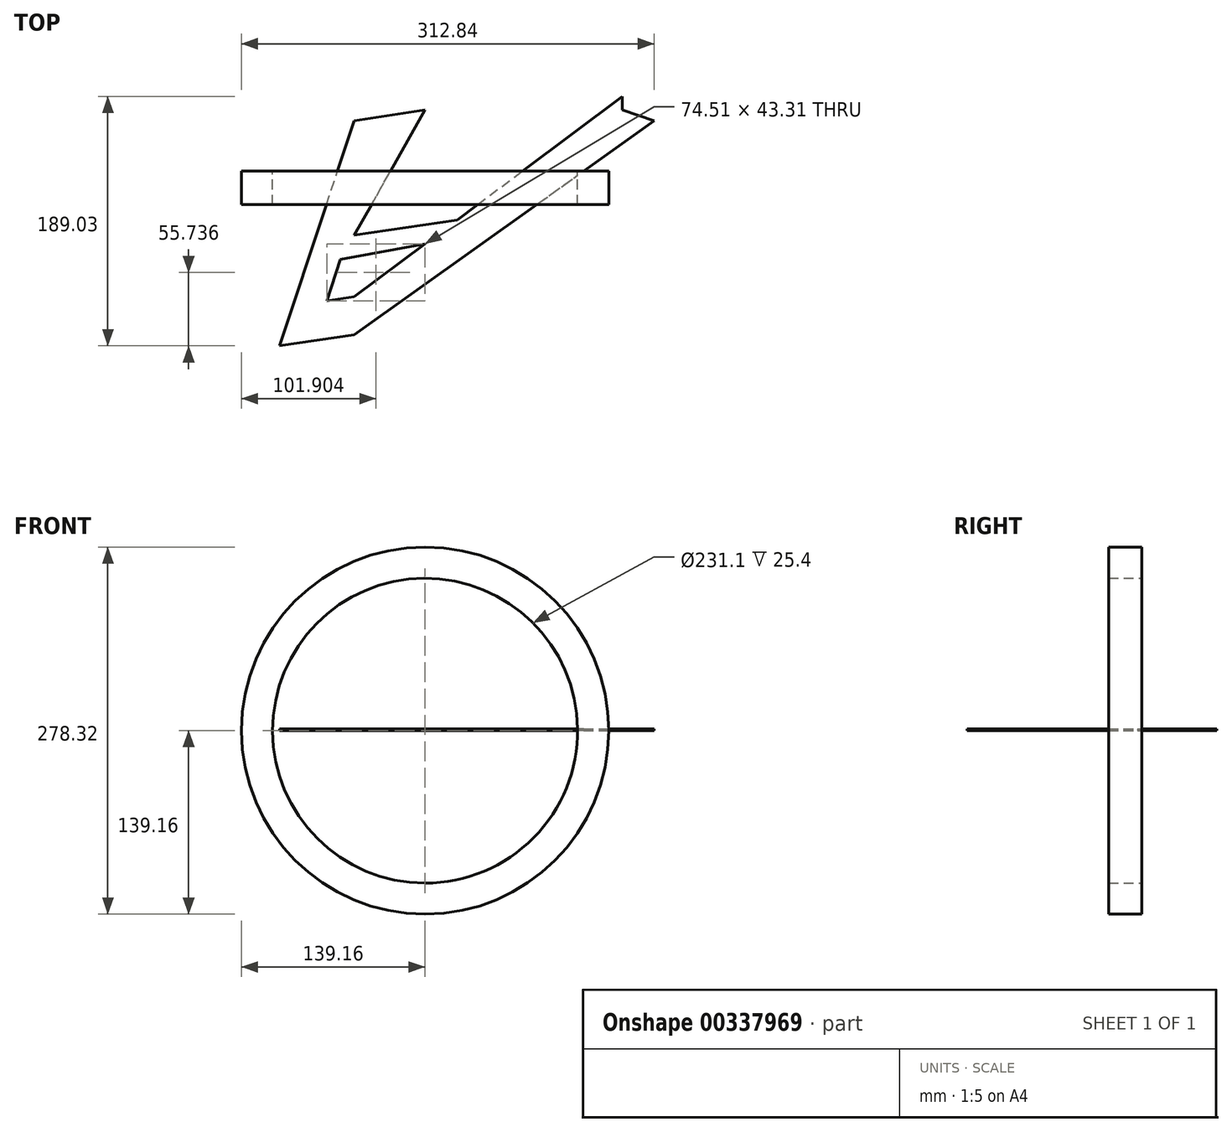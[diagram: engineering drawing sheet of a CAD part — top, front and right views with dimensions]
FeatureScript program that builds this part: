
annotation { "Feature Type Name" : "Feature", "Feature Type Description" : "" }
export const myFeature = defineFeature(function(context is Context, id is Id, definition is map)
    precondition{}
    {
        {
            var Q0;
            Q0=qCreatedBy(makeId("Front.planeOp"),FACE);
            var sketch = newSketch(context, id + "F0", { "sketchPlane" : qUnion([Q0])});
            skCircle(sketch, "E0", {"center": v(0, 0) * mm, "radius": 139.16 * mm});
            skCircle(sketch, "E1", {"center": v(0, 0) * mm, "radius": 115.55 * mm});
            skSolve(sketch);
        }
        {
            var Q0;
            Q0=makeQuery(id+"F0.imprint","IMPRINT",FACE,{"disambiguationData":[TD([[makeQuery(id+"F0.imprint","IMPRINT",EDGE,{"derivedFrom":sQuery(id+"F0.wireOp",EDGE,"E0")}),1.0]])]});
            extrude(context, id + "F1", {"entities" : qUnion([Q0]), "depth" : 25.4 * mm});
        }
        {
            var Q0;
            Q0=qCreatedBy(makeId("Top.planeOp"),FACE);
            var sketch = newSketch(context, id + "F2", { "sketchPlane" : qUnion([Q0])});
            skLineSegment(sketch, "E2", {"start": v(-110.22, -132.5) * mm, "end": v(-53.74, 38.2) * mm});
            skLineSegment(sketch, "E3", {"start": v(-110.22, -132.5) * mm, "end": v(-53.74, -124.02) * mm});
            skLineSegment(sketch, "E4", {"start": v(-53.74, -124.02) * mm, "end": v(173.68, 38.2) * mm});
            skLineSegment(sketch, "E5", {"start": v(-53.74, 38.2) * mm, "end": v(0, 46.28) * mm});
            skLineSegment(sketch, "E6", {"start": v(173.68, 38.2) * mm, "end": v(149.3, 46.28) * mm});
            skLineSegment(sketch, "E7", {"start": v(-74.51, -98.42) * mm, "end": v(-53.74, -95.3) * mm});
            skLineSegment(sketch, "E8", {"start": v(-74.51, -98.42) * mm, "end": v(-64.13, -67.03) * mm});
            skPoint(sketch, "E8.endSnap0", {"position": v(-64.13, -96.86) * mm});
            skLineSegment(sketch, "E9", {"start": v(-53.74, -95.3) * mm, "end": v(0, -55.11) * mm});
            skLineSegment(sketch, "E10", {"start": v(-64.13, -67.03) * mm, "end": v(0, -55.11) * mm});
            skLineSegment(sketch, "E11", {"start": v(-64.13, -67.03) * mm, "end": v(0, 46.28) * mm});
            skLineSegment(sketch, "E12", {"start": v(0, -55.11) * mm, "end": v(149.3, 56.53) * mm});
            skLineSegment(sketch, "E13", {"start": v(149.3, 56.53) * mm, "end": v(149.3, 46.28) * mm});
            skLineSegment(sketch, "E14", {"start": v(-53.74, -48.68) * mm, "end": v(24.25, -36.98) * mm});
            skSolve(sketch);
        }
        {
            var Q0;
            Q0=makeQuery(id+"F2.imprint","IMPRINT",FACE,{"disambiguationData":[TD([[makeQuery(id+"F2.imprint","IMPRINT",EDGE,{"derivedFrom":sQuery(id+"F2.wireOp",EDGE,"E2")}),-1.0]])]});
            var Q1;
            {var subQ0=sQuery(id+"F2.wireOp",EDGE,"E10");Q1=makeQuery(id+"F2.imprint","IMPRINT",FACE,{"disambiguationData":[TD([[makeQuery(id+"F2.imprint","IMPRINT",EDGE,{"derivedFrom":subQ0}),1.0]])]});}
            extrude(context, id + "F3", {"entities" : qUnion([Q0, Q1]), "operationType" : NewBodyOperationType.ADD, "depth" : 1.27 * mm});
        }
    });
